# Revit family: X554UNS
name_source: partatom
category: Specialty Equipment
revit_build: Autodesk Revit Architecture 2012 (Build: 20110309_2315(x64)
units: mm (PartAtom-declared; Revit-internal decimal feet)

## types (1)
- X554UNS
    Additional Features = See brochure
    Back Circuit Panel Height = 19.26 "
    Back Circuit Panel Height from Bottom = 3.09 "
    Back Circuit Panel Width = 35.43 "
    Connectivity- Input Terminals. Analog = VGA 15-pin D-sub, (shared S-Video, Video, Component), BNC Composite
    Connectivity- Input Terminals. Audio = Audio Mini-Jack, DisplayPort Audio, HDMI Audio
    Connectivity- Input Terminals. Digital = Display Port, HDMI, DVI-D
    Connectivity- Input Terminals. External Control = RS-232C, LAN, DDC/CI
    Connectivity- Output Terminals. Audio = Audio Mini-Jack, External Speaker Jack (2), HDMI Audio (through DisplayPort Out), DisplayPort Audio
    Connectivity- Output Terminals. Digital = DisplayPort (DisplayPort, HDMI, DVI-D or Option Signals out of this port)
    Connectivity- Output Terminals. External Control = LAN
    Connectivity- PC/Mac Signal Compatibility = Yes
    Environmental Conditions- Operating Altitude = 13,780ft / 4200m
    Environmental Conditions- Operating Humidity = 20-80%
    Environmental Conditions- Operating Temperature = 41-104 degF / 5-40 degC
    Height from Floor = 26 "
    LCD- Active Screen Area (W x H) = 47.6 x 26.8 in. / 1209.6 x 680.4 mm
    LCD- Aspect Ratio = 16 : 9
    LCD- Brightness (Typical/Max) = 500 / 700 cd/m2
    LCD- Contrast Ratio (Typical) = 3500 : 1
    LCD- Displayable Colors = More than 16.7 Million
    LCD- Native Resolution = 1920 x 1080
    LCD- Orientation = Landscape / Portrait
    LCD- Panel Technology = SPVA (P-DID)
    LCD- Response Time (white to black) = 8 ms
    LCD- Viewable Image Size = 55"
    LCD- Viewing Angle = 178deg Vert., 178deg Hor. (89U/89D/89L/89R) at CR>10
    Limited Warranty = 3 years parts and labor, including backlight
    Manufacturer = NEC Display
    Optional Accessories = See brochure
    Panel Height = 27.01 "
    Panel Thickness Back = 0.73 "
    Panel Thickness Front = 2.36 "
    Panel Thickness Overall = 3.92 "
    Panel Width = 0.15 "
    Panel Width Overall = 47.85 "
    Physical Specs- Bezel Width (L/R, T/B) = 0.09in/0.05in, 0.09in/0.05in; 2.3mm/1.2mm, 2.3mm/1.2mm
    Physical Specs- Net Dimensions (w/o stand- WxHxD) = 47.8 x 27 x 3.9in / 1215.3 x 686.1 x 99.6mm
    Physical Specs- Net Weight (w/o stand) = 61.5 lbs / 27.9 kgs
    Physical Specs- VESA Hole Configuration = 400 x 400mm (4-hole)
    Power Consumption- ECO Mode Standby = <0.5W
    Power Consumption- On (Typical) = 150W
    Ships with = See brochure
    URL = necdisplay.com
    c1 = 0.15 "
    c2 = 0.1 "

## geometry (parser evidence)
native form markers: Blend x9, Sweep x27
no freeform markers — native parametric forms only
